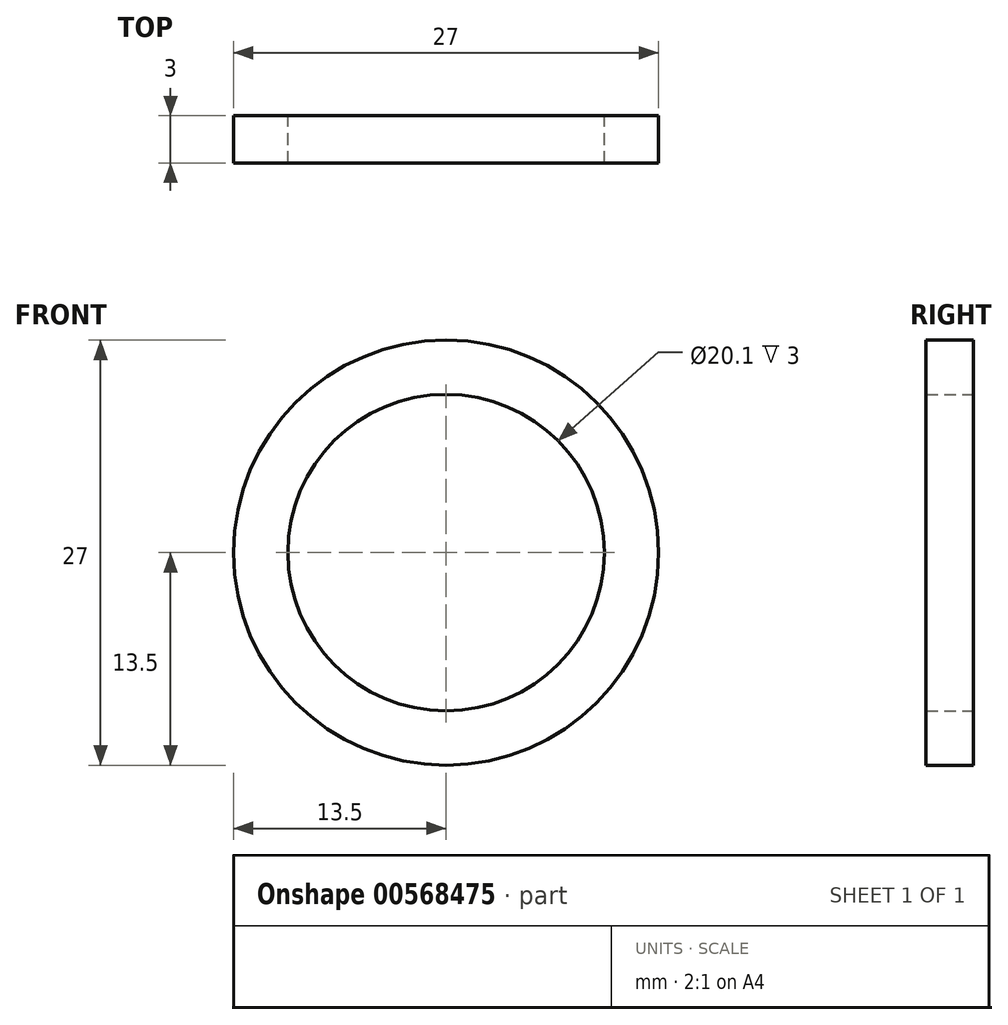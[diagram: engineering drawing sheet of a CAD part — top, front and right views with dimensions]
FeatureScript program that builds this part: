
annotation { "Feature Type Name" : "Feature", "Feature Type Description" : "" }
export const myFeature = defineFeature(function(context is Context, id is Id, definition is map)
    precondition{}
    {
        {
            var Q0;
            Q0=qCreatedBy(makeId("Front.planeOp"),FACE);
            var sketch = newSketch(context, id + "F0", { "sketchPlane" : qUnion([Q0])});
            skCircle(sketch, "E0", {"center": v(0, 0) * mm, "radius": 13.5 * mm});
            skCircle(sketch, "E1", {"center": v(0, 0) * mm, "radius": 10.05 * mm});
            skSolve(sketch);
        }
        {
            var Q0;
            Q0 = qSketchRegion(id + "F0", true);
            extrude(context, id + "F1", {"entities" : qUnion([Q0]), "depth" : 3 * mm, "offsetDistance" : 25.4 * mm});
        }
    });
